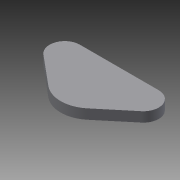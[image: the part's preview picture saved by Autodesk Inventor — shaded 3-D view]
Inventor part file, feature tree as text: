
AUTODESK INVENTOR PART (.ipt)
format: ipt  version: 2013 (Build 170138000, 138)  size: 110,592 bytes
history: native  units: mm
features: extrude x1, sketch x1
ambient origin geometry x8: Origin, YZ Plane, XZ Plane, XY Plane, X Axis, Y Axis, Z Axis, Center Point
feature tree (2):
  extrude  "Extrusion11"  Depth=3.0mm
  sketch  "Sketch1"  dims[d3=3.0mm d5=3.0mm d42=120.0mm d43=80.0mm d44=3.25mm d45=7.0mm d47=9.25mm d50=10.0mm d51=13.0mm d54=20.0mm d55=5.0mm d56=50.0mm d58=10.0mm d59=10.0mm d61=10.0mm d63=15.0mm d64=5.0mm d65=7.0mm d69=10.0mm d70=30.0mm d73=5.0mm d74=10.0mm d77=3.25mm d78=0.0mm]
